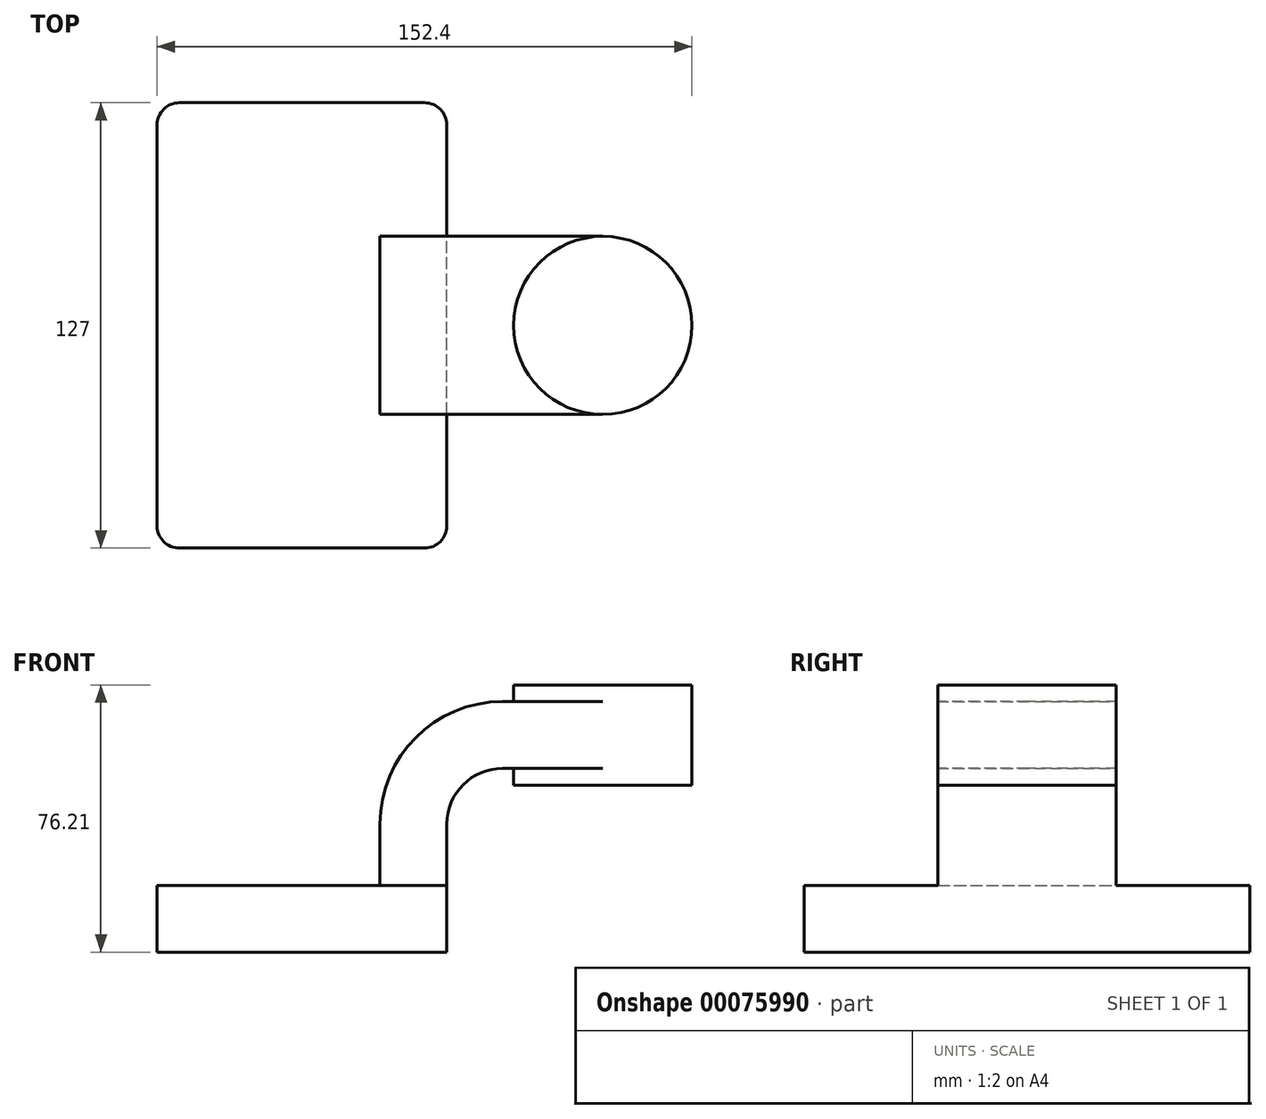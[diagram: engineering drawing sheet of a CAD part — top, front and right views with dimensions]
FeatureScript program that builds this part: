
annotation { "Feature Type Name" : "Feature", "Feature Type Description" : "" }
export const myFeature = defineFeature(function(context is Context, id is Id, definition is map)
    precondition{}
    {
        {
            var Q0;
            Q0=qCreatedBy(makeId("Front.planeOp"),FACE);
            var sketch = newSketch(context, id + "F0", { "sketchPlane" : qUnion([Q0])});
            skLineSegment(sketch, "E0.bottom", {"start": v(41.27, 9.53) * mm, "end": v(-41.28, 9.53) * mm});
            skLineSegment(sketch, "E0.top", {"start": v(41.28, -9.52) * mm, "end": v(-41.27, -9.52) * mm});
            skLineSegment(sketch, "E0.left", {"start": v(41.28, 9.53) * mm, "end": v(41.28, -9.52) * mm});
            skLineSegment(sketch, "E0.right", {"start": v(-41.28, 9.53) * mm, "end": v(-41.27, -9.52) * mm});
            skPoint(sketch, "E0.middle", {"position": v(0, 0) * mm});
            skLineSegment(sketch, "E1.bottom", {"start": v(111.12, 66.68) * mm, "end": v(60.32, 66.68) * mm});
            skLineSegment(sketch, "E1.top", {"start": v(111.12, 38.1) * mm, "end": v(60.32, 38.1) * mm});
            skLineSegment(sketch, "E1.left", {"start": v(111.12, 66.68) * mm, "end": v(111.12, 38.1) * mm});
            skLineSegment(sketch, "E1.right", {"start": v(60.32, 66.67) * mm, "end": v(60.32, 38.1) * mm});
            skPoint(sketch, "E1.middle", {"position": v(85.72, 52.39) * mm});
            skLineSegment(sketch, "E2", {"start": v(41.27, 9.53) * mm, "end": v(41.27, 26.99) * mm});
            skArc(sketch, "E3", {"start": v(41.27, 26.99) * mm, "mid": v(45.92, 38.21) * mm, "end": v(57.15, 42.86) * mm});
            skLineSegment(sketch, "E4", {"start": v(57.15, 42.86) * mm, "end": v(85.72, 42.86) * mm});
            skLineSegment(sketch, "E5.0", {"start": v(57.15, 61.91) * mm, "end": v(85.72, 61.91) * mm});
            skArc(sketch, "E5.1", {"start": v(22.23, 26.99) * mm, "mid": v(32.45, 51.68) * mm, "end": v(57.15, 61.91) * mm});
            skLineSegment(sketch, "E5.2", {"start": v(22.22, 9.53) * mm, "end": v(22.22, 26.99) * mm});
            skLineSegment(sketch, "E6", {"start": v(85.72, 38.1) * mm, "end": v(85.72, 66.68) * mm});
            skFitSpline(sketch, "E7", {"points": [v(-41.28, 9.53) * mm, v(57.15, 61.91) * mm], "startDerivative": vector(0.55, 98.01) * mm, "endDerivative": vector(151.57, -1.83) * mm});
            skSolve(sketch);
        }
        {
            var Q0;
            Q0=makeQuery(id+"F0.imprint","IMPRINT",FACE,{"disambiguationData":[TD([[makeQuery(id+"F0.imprint","IMPRINT",EDGE,{"derivedFrom":sQuery(id+"F0.wireOp",EDGE,"E0.top")}),-1.0]])]});
            extrude(context, id + "F1", {"entities" : qUnion([Q0]), "endBound" : BoundingType.SYMMETRIC, "depth" : 127 * mm});
        }
        {
            var Q0;
            {var subQ1=sQuery(id+"F0.wireOp",EDGE,"E2");Q0=makeQuery(id+"F0.imprint","IMPRINT",FACE,{"disambiguationData":[TD([[makeQuery(id+"F0.imprint","IMPRINT",EDGE,{"derivedFrom":subQ1}),1.0]])]});}
            var Q1;
            {var subQ0=sQuery(id+"F0.wireOp",EDGE,"E5.0");var subQ1=sQuery(id+"F0.wireOp",EDGE,"E1.right");var subQ2=makeQuery(id+"F0.imprint","INTERSECT",VERTEX,{"derivedFrom":[subQ1,subQ0]});Q1=makeQuery(id+"F0.imprint","IMPRINT",FACE,{"disambiguationData":[TD([[makeQuery(id+"F0.imprint","IMPRINT",EDGE,{"disambiguationData":[TD([[subQ2,-1.0]])],"derivedFrom":subQ1}),1.0]])]});}
            extrude(context, id + "F2", {"entities" : qUnion([Q0, Q1]), "operationType" : NewBodyOperationType.ADD, "endBound" : BoundingType.SYMMETRIC, "depth" : 50.8 * mm});
        }
        {
            var Q0;
            Q0=makeQuery(id+"F0.imprint","IMPRINT",FACE,{"disambiguationData":[TD([[makeQuery(id+"F0.imprint","IMPRINT",EDGE,{"derivedFrom":sQuery(id+"F0.wireOp",EDGE,"E5.1")}),1.0]])]});
            extrude(context, id + "F3", {"entities" : qUnion([Q0]), "operationType" : NewBodyOperationType.ADD, "endBound" : BoundingType.SYMMETRIC, "depth" : 15.88 * mm});
        }
        {
            var Q0;
            {var subQ0=sQuery(id+"F0.wireOp",EDGE,"E1.left");Q0=makeQuery(id+"F0.imprint","IMPRINT",FACE,{"disambiguationData":[TD([[makeQuery(id+"F0.imprint","IMPRINT",EDGE,{"derivedFrom":subQ0}),-1.0]])]});}
            var Q1;
            Q1=sQuery(id+"F0.wireOp",EDGE,"E6");
            revolve(context, id + "F4", {"operationType" : NewBodyOperationType.ADD, "entities" : qUnion([Q0]), "axis" : qUnion([Q1]), "revolveType" : RevolveType.FULL});
        }
        {
            var Q0;
            Q0=makeQuery(id+"F1.opExtrude","CAP_EDGE",EDGE,{"disambiguationData":[OSD([sQuery(id+"F0.wireOp",EDGE,"E0.left")])],"isStart":false});
            var Q1;
            Q1=makeQuery(id+"F1.opExtrude","CAP_EDGE",EDGE,{"disambiguationData":[OSD([sQuery(id+"F0.wireOp",EDGE,"E0.right")])],"isStart":false});
            var Q2;
            Q2=makeQuery(id+"F1.opExtrude","CAP_EDGE",EDGE,{"disambiguationData":[OSD([sQuery(id+"F0.wireOp",EDGE,"E0.left")])],"isStart":true});
            var Q3;
            Q3=makeQuery(id+"F1.opExtrude","CAP_EDGE",EDGE,{"disambiguationData":[OSD([sQuery(id+"F0.wireOp",EDGE,"E0.right")])],"isStart":true});
            fillet(context, id + "F5", {"entities" : qUnion([Q0, Q1, Q2, Q3]), "radius" : 6.35 * mm, "tangentPropagation" : true, "allowEdgeOverflow" : false});
        }
    });
